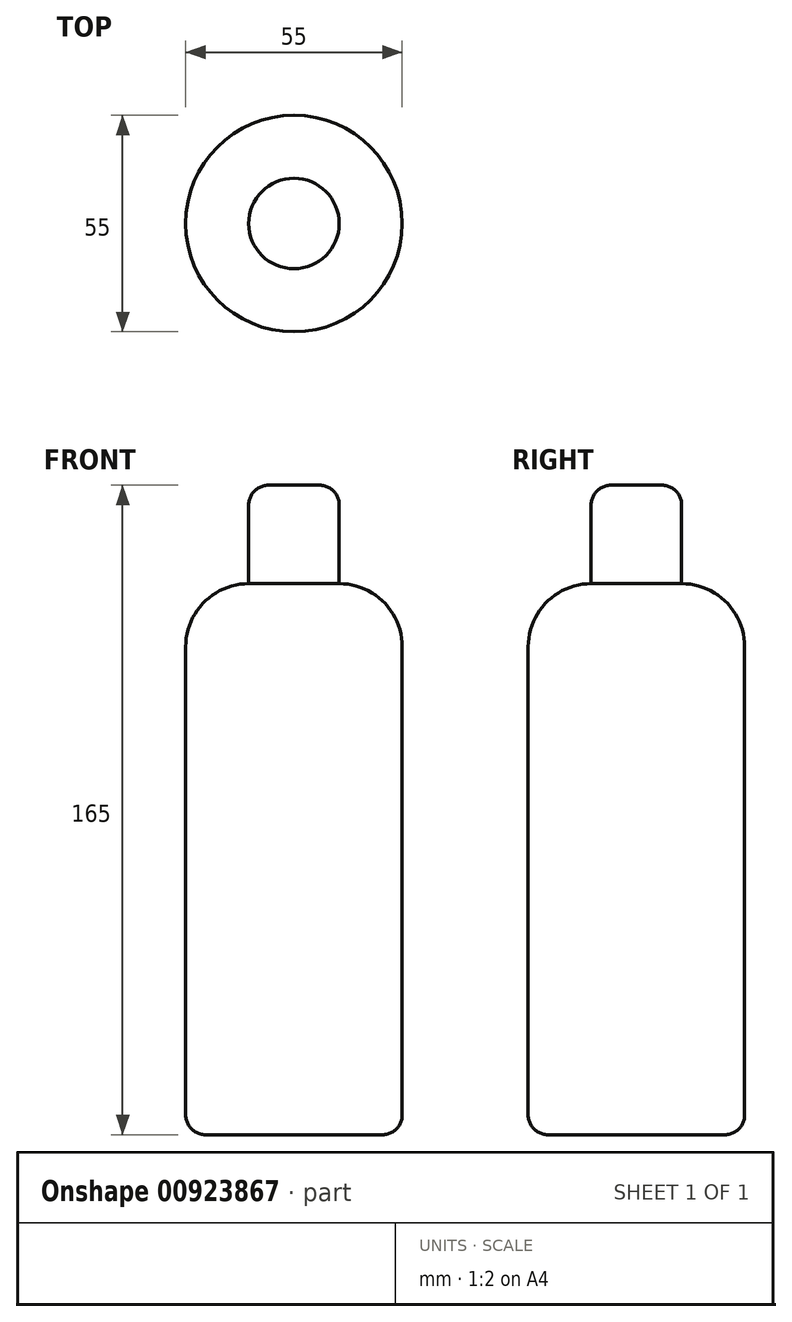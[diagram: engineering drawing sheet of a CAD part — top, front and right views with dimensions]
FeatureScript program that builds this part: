
annotation { "Feature Type Name" : "Feature", "Feature Type Description" : "" }
export const myFeature = defineFeature(function(context is Context, id is Id, definition is map)
    precondition{}
    {
        {
            var Q0;
            Q0=qCreatedBy(makeId("Front.planeOp"),FACE);
            var sketch = newSketch(context, id + "F0", { "sketchPlane" : qUnion([Q0])});
            skLineSegment(sketch, "E0", {"start": v(0, 0) * mm, "end": v(27.5, 0) * mm});
            skLineSegment(sketch, "E1", {"start": v(27.5, 0) * mm, "end": v(27.5, 124) * mm});
            skLineSegment(sketch, "E2", {"start": v(11.5, 140) * mm, "end": v(0, 140) * mm});
            skLineSegment(sketch, "E3", {"start": v(0, 140) * mm, "end": v(0, 0) * mm});
            skPoint(sketch, "E4.visualSharp", {"position": v(27.5, 140) * mm});
            skArc(sketch, "E4.filletArc", {"start": v(27.5, 124) * mm, "mid": v(22.81, 135.31) * mm, "end": v(11.5, 140) * mm});
            skSolve(sketch);
        }
        {
            var Q0;
            Q0=makeQuery(id+"F0.imprint","IMPRINT",FACE,{"disambiguationData":[TD([[makeQuery(id+"F0.imprint","IMPRINT",EDGE,{"derivedFrom":sQuery(id+"F0.wireOp",EDGE,"E0")}),1.0]])]});
            var Q1;
            Q1=sQuery(id+"F0.wireOp",EDGE,"E3");
            revolve(context, id + "F1", {"surfaceOperationType" : NewSurfaceOperationType.NEW, "entities" : qUnion([Q0]), "axis" : qUnion([Q1]), "revolveType" : RevolveType.FULL});
        }
        {
            var Q0;
            Q0=makeQuery(id+"F1.opRevolve","SWEPT_FACE",FACE,{"disambiguationData":[OSD([sQuery(id+"F0.wireOp",EDGE,"E2")])]});
            var sketch = newSketch(context, id + "F2", { "sketchPlane" : qUnion([Q0])});
            skCircle(sketch, "E5.0", {"center": v(0, 0) * mm, "radius": 11.5 * mm});
            skSolve(sketch);
        }
        {
            var Q0;
            Q0 = qSketchRegion(id + "F2", true);
            extrude(context, id + "F3", {"entities" : qUnion([Q0]), "operationType" : NewBodyOperationType.ADD, "depth" : 25 * mm, "offsetDistance" : 25 * mm});
        }
        {
            var Q0;
            Q0=makeQuery(id+"F3.opExtrude","CAP_EDGE",EDGE,{"disambiguationData":[OSD([sQuery(id+"F2.wireOp",EDGE,"E5.0")])],"isStart":false});
            fillet(context, id + "F4", {"entities" : qUnion([Q0]), "radius" : 5 * mm, "tangentPropagation" : true, "allowEdgeOverflow" : false});
        }
        {
            var Q0;
            Q0=makeQuery(id+"F1.opRevolve","SWEPT_EDGE",EDGE,{"disambiguationData":[OSD([sQuery(id+"F0.wireOp",EDGE,"E0"),sQuery(id+"F0.wireOp",EDGE,"E1")])]});
            fillet(context, id + "F5", {"entities" : qUnion([Q0]), "radius" : 5 * mm, "tangentPropagation" : true, "allowEdgeOverflow" : false});
        }
    });
